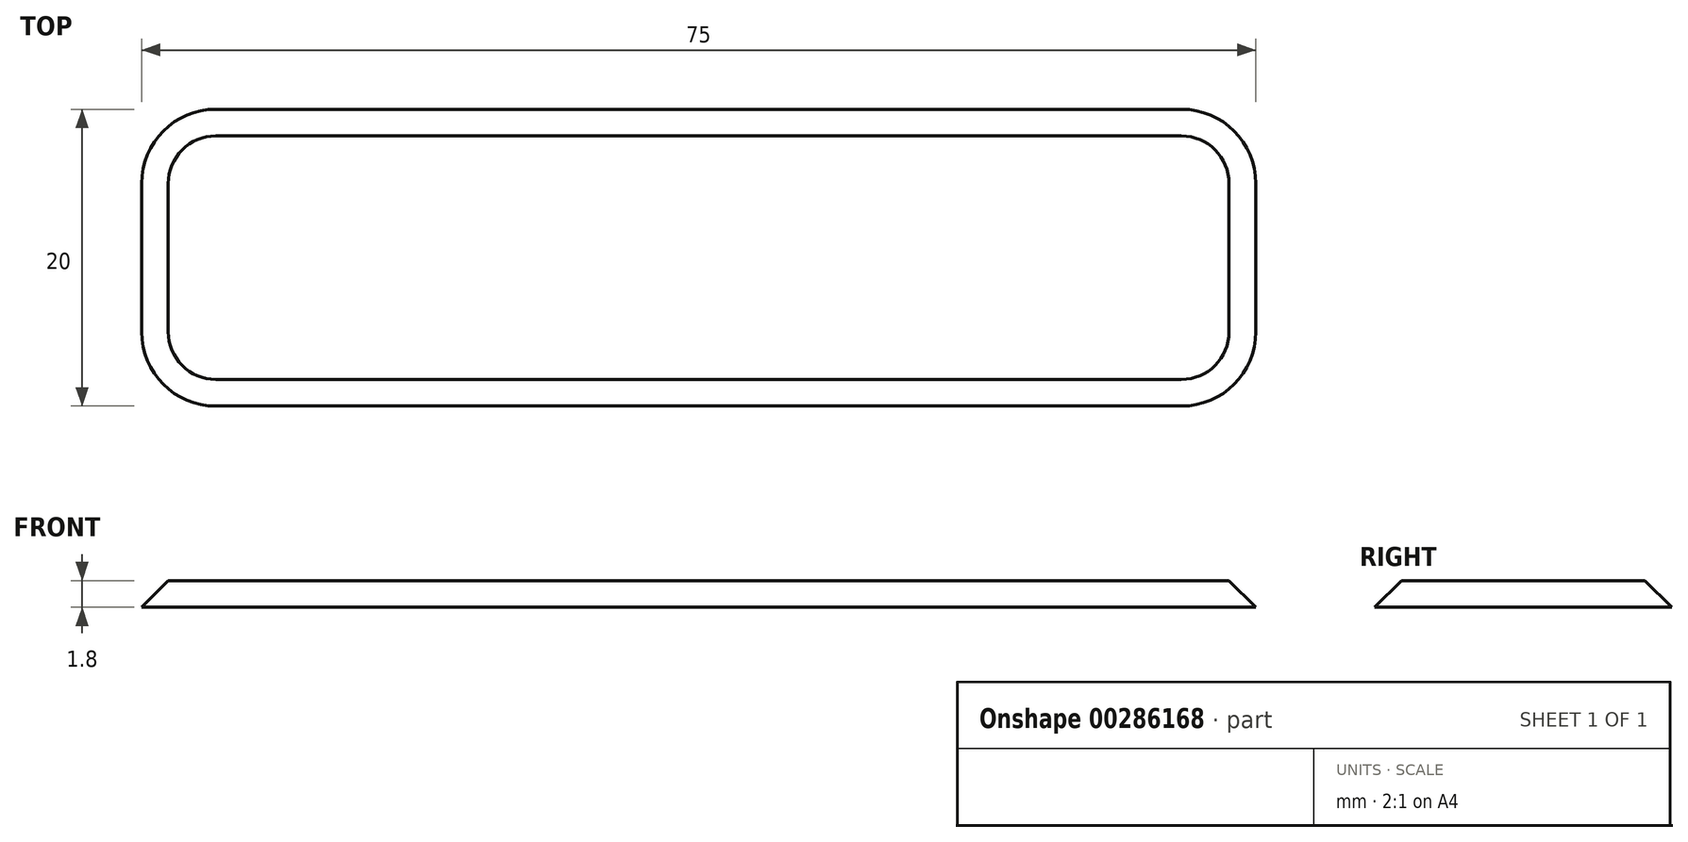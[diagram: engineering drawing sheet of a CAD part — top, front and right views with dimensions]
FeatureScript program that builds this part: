
annotation { "Feature Type Name" : "Feature", "Feature Type Description" : "" }
export const myFeature = defineFeature(function(context is Context, id is Id, definition is map)
    precondition{}
    {
        {
            var Q0;
            Q0=qCreatedBy(makeId("Top.planeOp"),FACE);
            var sketch = newSketch(context, id + "F0", { "sketchPlane" : qUnion([Q0])});
            skLineSegment(sketch, "E0.bottom", {"start": v(37.5, -10) * mm, "end": v(-37.5, -10) * mm});
            skLineSegment(sketch, "E0.top", {"start": v(37.5, 10) * mm, "end": v(-37.5, 10) * mm});
            skLineSegment(sketch, "E0.left", {"start": v(37.5, -10) * mm, "end": v(37.5, 10) * mm});
            skLineSegment(sketch, "E0.right", {"start": v(-37.5, -10) * mm, "end": v(-37.5, 10) * mm});
            skPoint(sketch, "E0.middle", {"position": v(0, 0) * mm});
            skSolve(sketch);
        }
        {
            var Q0;
            Q0=makeQuery(id+"F0.imprint","IMPRINT",FACE,{"disambiguationData":[TD([[makeQuery(id+"F0.imprint","IMPRINT",EDGE,{"derivedFrom":sQuery(id+"F0.wireOp",EDGE,"E0.bottom")}),-1.0]])]});
            extrude(context, id + "F1", {"entities" : qUnion([Q0]), "depth" : 1.8 * mm});
        }
        {
            var Q0;
            Q0=makeQuery(id+"F1.opExtrude","SWEPT_EDGE",EDGE,{"disambiguationData":[OSD([sQuery(id+"F0.wireOp",EDGE,"E0.bottom"),sQuery(id+"F0.wireOp",EDGE,"E0.right")])]});
            var Q1;
            Q1=makeQuery(id+"F1.opExtrude","SWEPT_EDGE",EDGE,{"disambiguationData":[OSD([sQuery(id+"F0.wireOp",EDGE,"E0.top"),sQuery(id+"F0.wireOp",EDGE,"E0.right")])]});
            var Q2;
            Q2=makeQuery(id+"F1.opExtrude","SWEPT_EDGE",EDGE,{"disambiguationData":[OSD([sQuery(id+"F0.wireOp",EDGE,"E0.bottom"),sQuery(id+"F0.wireOp",EDGE,"E0.left")])]});
            var Q3;
            Q3=makeQuery(id+"F1.opExtrude","SWEPT_EDGE",EDGE,{"disambiguationData":[OSD([sQuery(id+"F0.wireOp",EDGE,"E0.top"),sQuery(id+"F0.wireOp",EDGE,"E0.left")])]});
            fillet(context, id + "F2", {"entities" : qUnion([Q0, Q1, Q2, Q3]), "radius" : 5 * mm, "tangentPropagation" : true, "allowEdgeOverflow" : false});
        }
        {
            var Q0;
            Q0=makeQuery(id+"F1.opExtrude","CAP_FACE",FACE,{"disambiguationData":[OSD([sQuery(id+"F0.wireOp",EDGE,"E0.bottom"),sQuery(id+"F0.wireOp",EDGE,"E0.top"),sQuery(id+"F0.wireOp",EDGE,"E0.left"),sQuery(id+"F0.wireOp",EDGE,"E0.right")])],"isStart":false});
            chamfer(context, id + "F3", {"entities" : qUnion([Q0]), "width" : 1.8 * mm, "tangentPropagation" : true});
        }
    });
